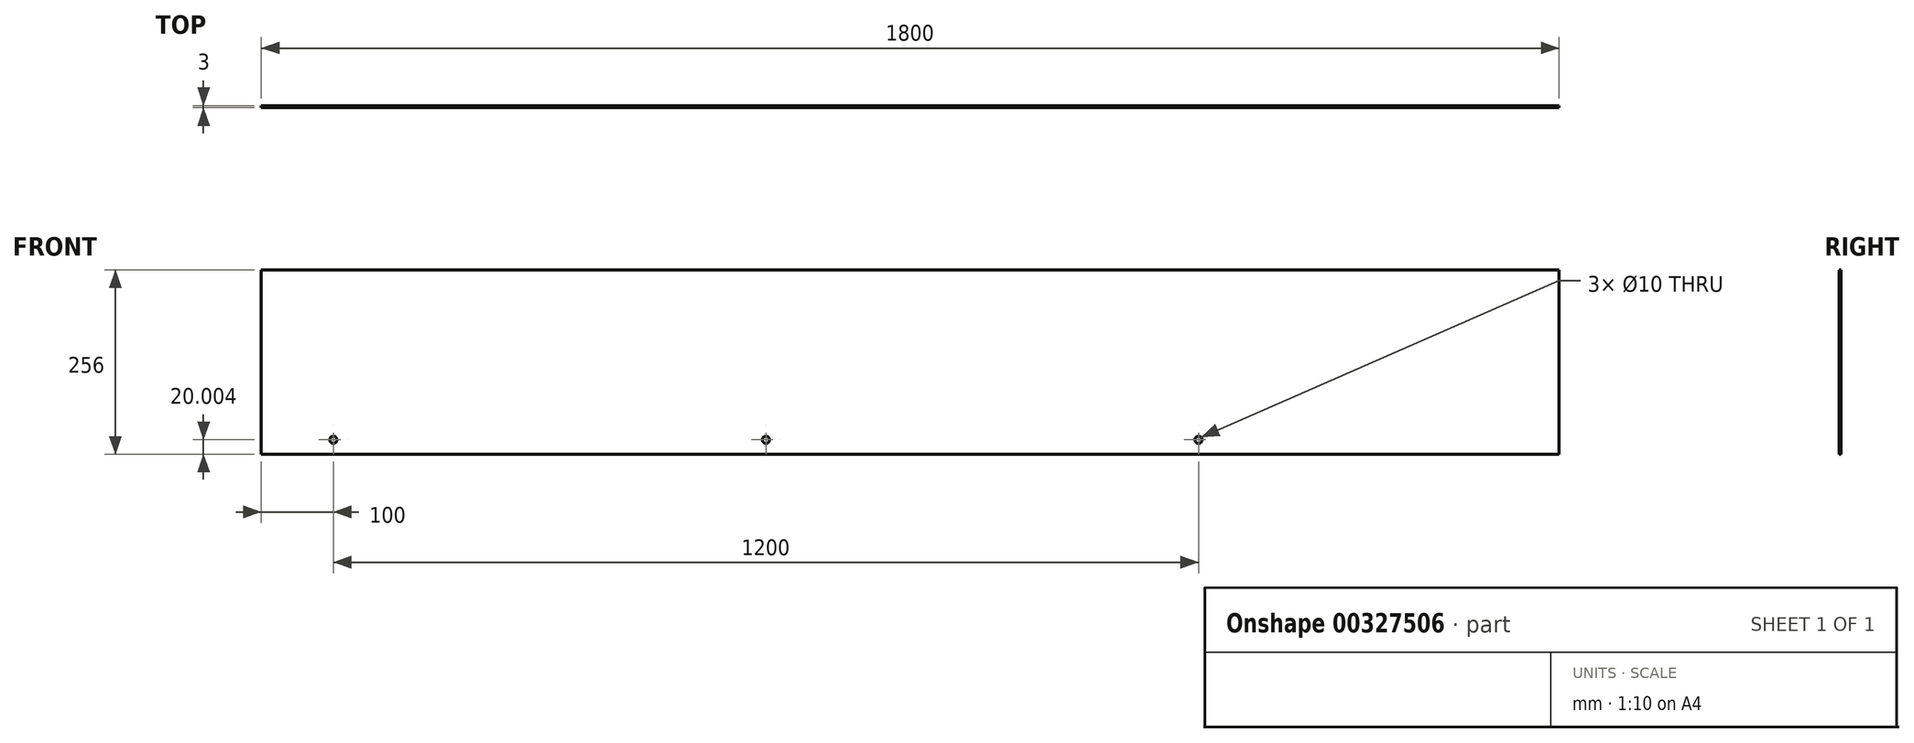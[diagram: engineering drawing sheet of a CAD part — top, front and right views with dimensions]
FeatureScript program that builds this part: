
annotation { "Feature Type Name" : "Feature", "Feature Type Description" : "" }
export const myFeature = defineFeature(function(context is Context, id is Id, definition is map)
    precondition{}
    {
        {
            var Q0;
            Q0=qCreatedBy(makeId("Front.planeOp"),FACE);
            var sketch = newSketch(context, id + "F0", { "sketchPlane" : qUnion([Q0])});
            skLineSegment(sketch, "E0", {"start": v(1913.88, -0.06) * mm, "end": v(1913.88, 255.94) * mm});
            skLineSegment(sketch, "E1", {"start": v(1913.88, -0.06) * mm, "end": v(113.88, -0.06) * mm});
            skLineSegment(sketch, "E2", {"start": v(113.88, -0.06) * mm, "end": v(113.88, 255.94) * mm});
            skLineSegment(sketch, "E3", {"start": v(113.88, 255.94) * mm, "end": v(1913.88, 255.94) * mm});
            skLineSegment(sketch, "E4", {"start": v(1913.88, 19.94) * mm, "end": v(1413.88, 19.94) * mm, "construction": true});
            skCircle(sketch, "E5", {"center": v(1413.88, 19.94) * mm, "radius": 5 * mm});
            skCircle(sketch, "E6", {"center": v(213.88, 19.94) * mm, "radius": 5 * mm});
            skCircle(sketch, "E7", {"center": v(813.88, 19.94) * mm, "radius": 5 * mm});
            skLineSegment(sketch, "E8", {"start": v(1013.88, -0.06) * mm, "end": v(1013.88, 61.63) * mm, "construction": true});
            skSolve(sketch);
        }
        {
            var Q0;
            Q0 = qSketchRegion(id + "F0", true);
            extrude(context, id + "F1", {"entities" : qUnion([Q0]), "depth" : 3 * mm});
        }
    });
